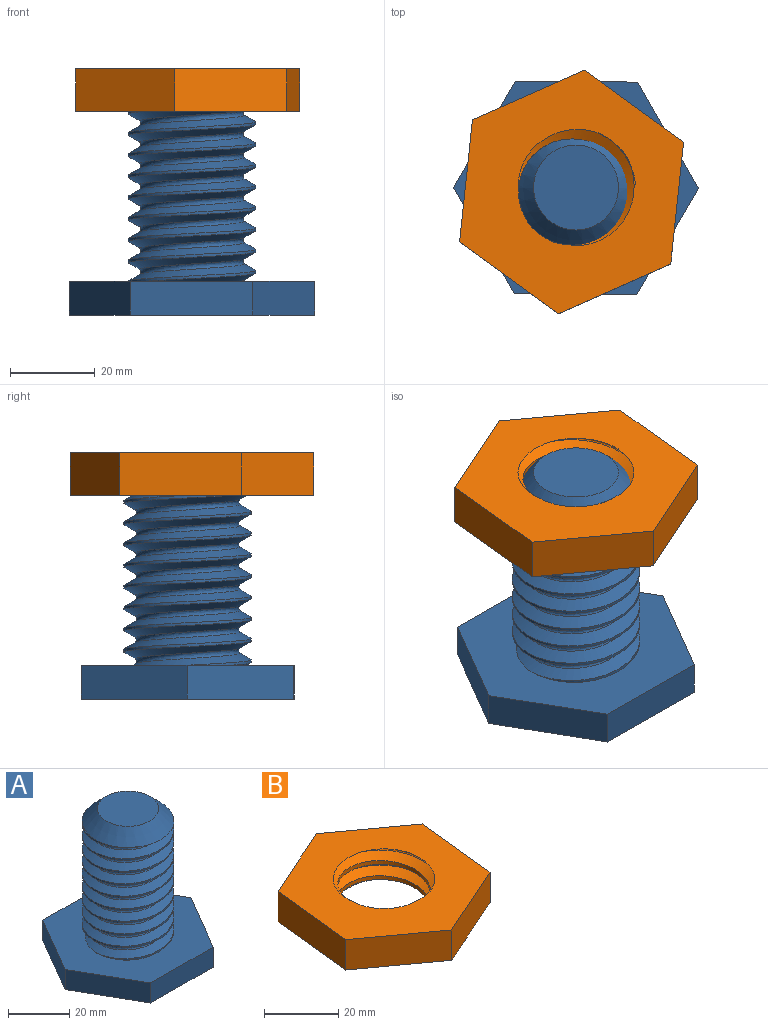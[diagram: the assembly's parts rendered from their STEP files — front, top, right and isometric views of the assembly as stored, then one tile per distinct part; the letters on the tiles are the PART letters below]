
ASSEMBLY  parts=2 mates=1
PART A: 15 faces, bbox 59.1x51.5x59.4 mm
  f0: plane 28.87x8mm, normal (0,1,0), area 230.9mm2, adj f1,f5,f6,f7
  f1: plane 24.93x14.55mm, normal (-0.86,0.5,0), area 230.9mm2, adj f0,f2,f6,f7
  f2: plane 25.07x14.32mm, normal (-0.87,-0.5,0), area 230.9mm2, adj f1,f3,f6,f7
  f3: plane 28.87x8mm, normal (0,-1,0), area 230.9mm2, adj f2,f4,f6,f7
  f4: plane 24.93x14.55mm, normal (0.86,-0.5,0), area 230.9mm2, adj f3,f5,f6,f7
  f5: plane 25.07x14.32mm, normal (0.87,0.5,0), area 230.9mm2, adj f0,f4,f6,f7
  f6: plane 59.12x51.52mm, normal (0,0,1), area 1594.7mm2, adj f0,f1,f2,f3,f4,f5,f8,f11
  f7: plane 57.73x50.14mm, normal (0,0,-1), area 2165.1mm2, adj f0,f1,f2,f3,f4,f5
  f8: cylinder r=15mm len=45mm, axis (0,0,-1), area 875.9mm2, adj f6,f10,f12,f13
  f9: plane 20x20mm, normal (0,0,1), area 314.2mm2, adj f10
  f10: cone r=10mm half-angle=45deg, axis (0,0,-1), area 555.4mm2, adj f8,f9,f14
  f11: bspline ~48.75x28.39mm, area 957.3mm2, adj f6,f12,f13,f14
  f12: bspline ~49.06x34.64mm, area 2412.4mm2, adj f6,f8,f11,f14
  f13: bspline ~48.23x34.64mm, area 2420.8mm2, adj f6,f8,f11,f14
  f14: plane 31.38x31.38mm, normal (0,0,-1), area 136.5mm2, adj f10,f11,f12,f13
PART B: 12 faces, bbox 53x57.7x14.3 mm
  f0: plane 23.35x16.98mm, normal (0.59,0.81,0), area 288.7mm2, adj f1,f5,f6,f7
  f1: plane 26.38x11.73mm, normal (-0.41,0.91,0), area 288.7mm2, adj f0,f2,f6,f7
  f2: plane 28.71x10mm, normal (-0.99,0.1,0), area 288.7mm2, adj f1,f3,f6,f7
  f3: plane 23.35x16.98mm, normal (-0.59,-0.81,0), area 288.7mm2, adj f2,f4,f6,f7
  f4: plane 26.38x11.73mm, normal (0.41,-0.91,0), area 288.7mm2, adj f3,f5,f6,f7
  f5: plane 28.71x10mm, normal (0.99,-0.1,0), area 288.7mm2, adj f0,f4,f6,f7
  f6: plane 57.68x53.02mm, normal (0,0,1), area 1572.3mm2, adj f0,f1,f2,f3,f4,f5,f8,f9
  f7: plane 57.68x53.02mm, normal (0,0,-1), area 1572.3mm2, adj f0,f1,f2,f3,f4,f5,f8,f9
  f8: bspline ~35.12x30.41mm, area 544.8mm2, adj f6,f7,f10,f11
  f9: bspline ~35.12x30.41mm, area 544.5mm2, adj f6,f7,f10,f11
  f10: bspline ~35.64x30.87mm, area 139.4mm2, adj f6,f7,f8,f9
  f11: cylinder r=12.5mm len=25mm, axis (0,0,1), area 196.2mm2, adj f6,f7,f8,f9
PLACE A t=(-16.77,5.14,-6.76)mm
PLACE B t=(-17.81,4.1,41.24)mm
MATE revolute B.f6 <-> A.f8  axis (0,0,1) through (-16.77,5.14,51.24)mm
